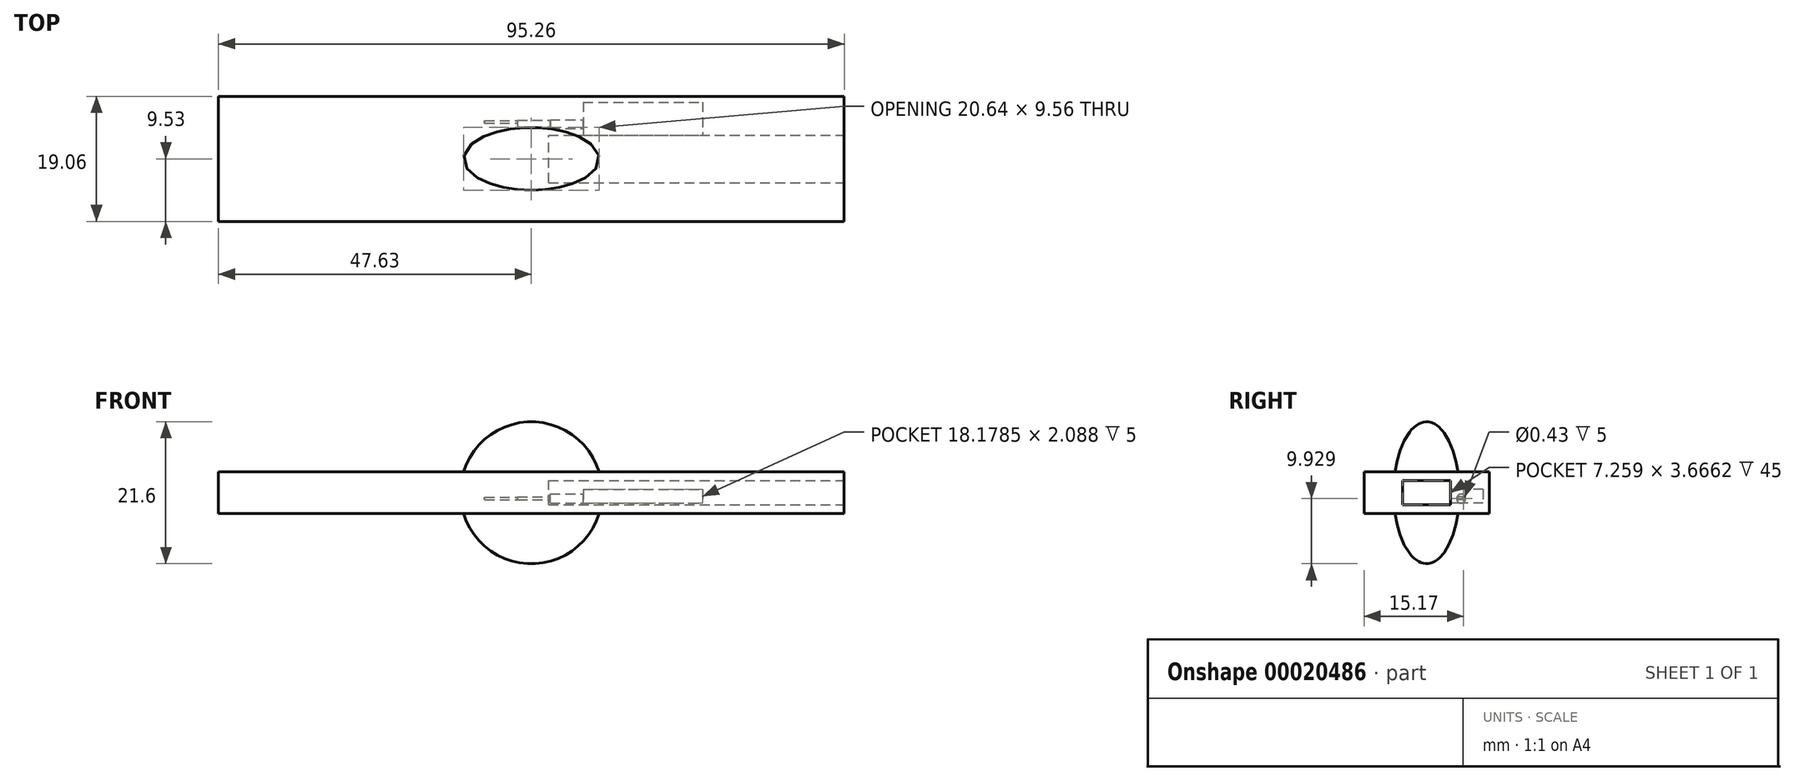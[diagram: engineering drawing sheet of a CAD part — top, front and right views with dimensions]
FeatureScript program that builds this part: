
annotation { "Feature Type Name" : "Feature", "Feature Type Description" : "" }
export const myFeature = defineFeature(function(context is Context, id is Id, definition is map)
    precondition{}
    {
        {
            var Q0;
            Q0=qCreatedBy(makeId("Top.planeOp"),FACE);
            var sketch = newSketch(context, id + "F0", { "sketchPlane" : qUnion([Q0])});
            skLineSegment(sketch, "E0.rect.bottom", {"start": v(47.63, 9.53) * mm, "end": v(-47.62, 9.52) * mm});
            skLineSegment(sketch, "E0.rect.top", {"start": v(47.63, -9.52) * mm, "end": v(-47.62, -9.53) * mm});
            skLineSegment(sketch, "E0.rect.left", {"start": v(47.63, 9.53) * mm, "end": v(47.63, -9.52) * mm});
            skLineSegment(sketch, "E0.rect.right", {"start": v(-47.62, 9.52) * mm, "end": v(-47.62, -9.53) * mm});
            skPoint(sketch, "E0.rect.middle", {"position": v(0, 0) * mm});
            skSolve(sketch);
        }
        {
            var Q0;
            Q0 = qSketchRegion(id + "F0", true);
            extrude(context, id + "F1", {"entities" : qUnion([Q0]), "endBound" : BoundingType.SYMMETRIC, "depth" : 6.35 * mm});
        }
        {
            var Q0;
            Q0=qCreatedBy(makeId("Top.planeOp"),FACE);
            var sketch = newSketch(context, id + "F2", { "sketchPlane" : qUnion([Q0])});
            skEllipticalArc(sketch, "E1", {});
            skLineSegment(sketch, "E2", {"start": v(0, 9.12) * mm, "end": v(0, -9.92) * mm, "construction": true});
            skLineSegment(sketch, "E3", {"start": v(0, 5) * mm, "end": v(0, -5) * mm});
            const initialGuessF2  = {"E1": [0, 0, 1, 0, 0.010797093901484906, 0.005, 4.71238898038469, 1.5707963267948966]};
            skSetInitialGuess(sketch, initialGuessF2);
            skSolve(sketch);
        }
        {
            var Q0;
            Q0 = qSketchRegion(id + "F2", true);
            var Q1;
            Q1=sQuery(id+"F2.wireOp",EDGE,"E2");
            revolve(context, id + "F3", {"operationType" : NewBodyOperationType.ADD, "entities" : qUnion([Q0]), "axis" : qUnion([Q1]), "revolveType" : RevolveType.FULL});
        }
        {
            var Q0;
            Q0=makeQuery(id+"F1.opExtrude","SWEPT_FACE",FACE,{"disambiguationData":[OSD([sQuery(id+"F0.wireOp",EDGE,"E0.rect.left")])]});
            var sketch = newSketch(context, id + "F4", { "sketchPlane" : qUnion([Q0])});
            skLineSegment(sketch, "E4.rect.bottom", {"start": v(-3.63, -1.83) * mm, "end": v(3.63, -1.83) * mm});
            skLineSegment(sketch, "E4.rect.top", {"start": v(-3.63, 1.83) * mm, "end": v(3.63, 1.83) * mm});
            skLineSegment(sketch, "E4.rect.left", {"start": v(-3.63, -1.83) * mm, "end": v(-3.63, 1.83) * mm});
            skLineSegment(sketch, "E4.rect.right", {"start": v(3.63, -1.83) * mm, "end": v(3.63, 1.83) * mm});
            skPoint(sketch, "E4.rect.middle", {"position": v(0, 0) * mm});
            skSolve(sketch);
        }
        {
            var Q0;
            Q0=makeQuery(id+"F4.imprint","IMPRINT",FACE,{"disambiguationData":[TD([[makeQuery(id+"F4.imprint","IMPRINT",EDGE,{"derivedFrom":sQuery(id+"F4.wireOp",EDGE,"E4.rect.bottom")}),1.0]])]});
            extrude(context, id + "F5", {"entities" : qUnion([Q0]), "operationType" : NewBodyOperationType.REMOVE, "oppositeDirection" : true, "depth" : 45 * mm});
        }
        {
            var Q0;
            Q0=makeQuery(id+"F5.boolean.opBoolean","COPY",FACE,{"derivedFrom":makeQuery(id+"F5.opExtrude","SWEPT_FACE",FACE,{"disambiguationData":[OSD([sQuery(id+"F4.wireOp",EDGE,"E4.rect.right")])]})});
            var sketch = newSketch(context, id + "F6", { "sketchPlane" : qUnion([Q0])});
            skLineSegment(sketch, "E5.rect.bottom", {"start": v(7.88, 0.5) * mm, "end": v(26.06, 0.5) * mm});
            skLineSegment(sketch, "E5.rect.top", {"start": v(7.88, -1.58) * mm, "end": v(26.06, -1.58) * mm});
            skLineSegment(sketch, "E5.rect.left", {"start": v(7.88, 0.5) * mm, "end": v(7.88, -1.58) * mm});
            skLineSegment(sketch, "E5.rect.right", {"start": v(26.06, 0.5) * mm, "end": v(26.06, -1.58) * mm});
            skPoint(sketch, "E5.rect.middle", {"position": v(16.97, -0.54) * mm});
            skSolve(sketch);
        }
        {
            var Q0;
            Q0 = qSketchRegion(id + "F6", true);
            extrude(context, id + "F7", {"entities" : qUnion([Q0]), "operationType" : NewBodyOperationType.REMOVE, "oppositeDirection" : true, "depth" : 5 * mm});
        }
        {
            var Q0;
            Q0=makeQuery(id+"F7.boolean.opBoolean","COPY",FACE,{"derivedFrom":makeQuery(id+"F7.opExtrude","SWEPT_FACE",FACE,{"disambiguationData":[OSD([sQuery(id+"F6.wireOp",EDGE,"E5.rect.left")])]})});
            var sketch = newSketch(context, id + "F8", { "sketchPlane" : qUnion([Q0])});
            skCircle(sketch, "E6", {"center": v(5.27, -0.9) * mm, "radius": 0.69 * mm});
            skPoint(sketch, "E6.first.point", {"position": v(5.31, -1.58) * mm});
            skPoint(sketch, "E6.second.point", {"position": v(5.08, -0.24) * mm});
            skPoint(sketch, "E6.third.point", {"position": v(5.85, -0.54) * mm});
            skSolve(sketch);
        }
        {
            var Q0;
            Q0 = qSketchRegion(id + "F8", true);
            extrude(context, id + "F9", {"entities" : qUnion([Q0]), "operationType" : NewBodyOperationType.REMOVE, "oppositeDirection" : true, "depth" : 5 * mm});
        }
        {
            var Q0;
            Q0=makeQuery(id+"F9.boolean.opBoolean","COPY",FACE,{"derivedFrom":makeQuery(id+"F9.opExtrude","CAP_FACE",FACE,{"disambiguationData":[OSD([sQuery(id+"F8.wireOp",EDGE,"E6")])],"isStart":false})});
            var sketch = newSketch(context, id + "F10", { "sketchPlane" : qUnion([Q0])});
            skLineSegment(sketch, "E7.bottom", {"start": v(5.86, -1.1) * mm, "end": v(4.84, -1.1) * mm});
            skLineSegment(sketch, "E7.top", {"start": v(5.86, -0.6) * mm, "end": v(4.84, -0.6) * mm});
            skLineSegment(sketch, "E7.left", {"start": v(5.86, -1.1) * mm, "end": v(5.86, -0.6) * mm});
            skLineSegment(sketch, "E7.right", {"start": v(4.84, -1.1) * mm, "end": v(4.84, -0.6) * mm});
            skSolve(sketch);
        }
        {
            var Q0;
            Q0 = qSketchRegion(id + "F10", true);
            extrude(context, id + "F11", {"entities" : qUnion([Q0]), "operationType" : NewBodyOperationType.REMOVE, "oppositeDirection" : true, "depth" : 5 * mm});
        }
        {
            var Q0;
            Q0=makeQuery(id+"F11.boolean.opBoolean","COPY",FACE,{"derivedFrom":makeQuery(id+"F11.opExtrude","CAP_FACE",FACE,{"disambiguationData":[OSD([sQuery(id+"F10.wireOp",EDGE,"E7.bottom"),sQuery(id+"F10.wireOp",EDGE,"E7.top"),sQuery(id+"F10.wireOp",EDGE,"E7.left"),sQuery(id+"F10.wireOp",EDGE,"E7.right")])],"isStart":false})});
            var sketch = newSketch(context, id + "F12", { "sketchPlane" : qUnion([Q0])});
            skCircle(sketch, "E8", {"center": v(5.64, -0.87) * mm, "radius": 0.21 * mm});
            skSolve(sketch);
        }
        {
            var Q0;
            Q0 = qSketchRegion(id + "F12", true);
            extrude(context, id + "F13", {"entities" : qUnion([Q0]), "operationType" : NewBodyOperationType.REMOVE, "oppositeDirection" : true, "depth" : 5 * mm});
        }
    });
